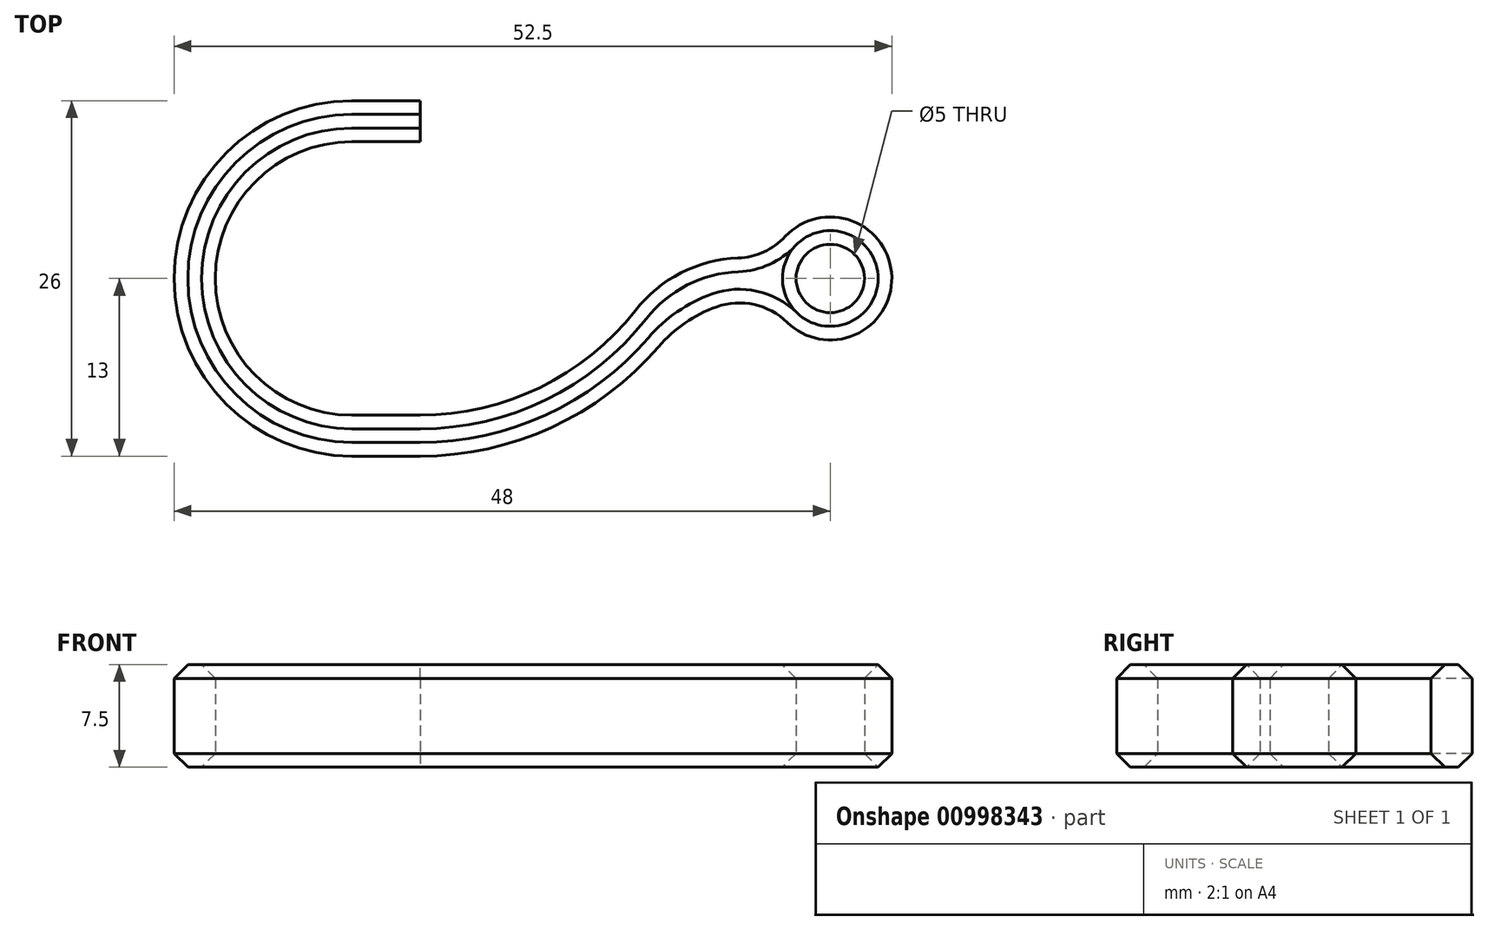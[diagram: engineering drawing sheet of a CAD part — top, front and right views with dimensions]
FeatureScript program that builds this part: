
annotation { "Feature Type Name" : "Feature", "Feature Type Description" : "" }
export const myFeature = defineFeature(function(context is Context, id is Id, definition is map)
    precondition{}
    {
        {
            var Q0;
            Q0=qCreatedBy(makeId("Top.planeOp"),FACE);
            var sketch = newSketch(context, id + "F0", { "sketchPlane" : qUnion([Q0])});
            skArc(sketch, "E0", {"start": v(0, 10) * mm, "mid": v(-10, 0) * mm, "end": v(0, -10) * mm});
            skArc(sketch, "E1", {"start": v(0, 13) * mm, "mid": v(-13, 0) * mm, "end": v(0, -13) * mm});
            skCircle(sketch, "E2", {"center": v(35, 0) * mm, "radius": 2.5 * mm});
            skArc(sketch, "E3", {"start": v(30.76, -1.5) * mm, "mid": v(39.5, 0) * mm, "end": v(30.76, 1.5) * mm});
            skPoint(sketch, "E4.middle", {"position": v(34.86, 0) * mm});
            skLineSegment(sketch, "E5", {"start": v(5, 13) * mm, "end": v(0, 13) * mm});
            skLineSegment(sketch, "E6", {"start": v(5, 10) * mm, "end": v(0, 10) * mm});
            skLineSegment(sketch, "E7", {"start": v(5, 13) * mm, "end": v(5, 10) * mm});
            skArc(sketch, "E8", {"start": v(5, -10) * mm, "mid": v(13.76, -7.98) * mm, "end": v(20.74, -2.33) * mm});
            skLineSegment(sketch, "E9", {"start": v(0, -13) * mm, "end": v(5, -13) * mm});
            skLineSegment(sketch, "E10", {"start": v(5, -10) * mm, "end": v(0, -10) * mm});
            skArc(sketch, "E11", {"start": v(5, -13) * mm, "mid": v(14.6, -10.9) * mm, "end": v(22.45, -4.98) * mm});
            skLineSegment(sketch, "E12.trimOffspring", {"start": v(30.76, 1.5) * mm, "end": v(28.62, 1.5) * mm});
            skLineSegment(sketch, "E13.trimOffspring", {"start": v(30.76, -1.5) * mm, "end": v(30.03, -1.5) * mm});
            skPoint(sketch, "E14.visualSharp", {"position": v(24.92, -1.5) * mm});
            skArc(sketch, "E14.filletArc", {"start": v(30.03, -1.5) * mm, "mid": v(25.86, -2.41) * mm, "end": v(22.45, -4.98) * mm});
            skPoint(sketch, "E15.visualSharp", {"position": v(23.1, 1.5) * mm});
            skArc(sketch, "E15.filletArc", {"start": v(28.62, 1.5) * mm, "mid": v(24.24, 0.5) * mm, "end": v(20.74, -2.33) * mm});
            skSolve(sketch);
        }
        {
            var Q0;
            Q0 = qSketchRegion(id + "F0", true);
            extrude(context, id + "F1", {"entities" : qUnion([Q0]), "endBound" : BoundingType.SYMMETRIC, "depth" : 7.5 * mm, "offsetDistance" : 25 * mm});
        }
        {
            var Q0;
            Q0=makeQuery(id+"F1.opExtrude","SWEPT_EDGE",EDGE,{"disambiguationData":[OSD([sQuery(id+"F0.wireOp",EDGE,"E3"),sQuery(id+"F0.wireOp",EDGE,"E13.trimOffspring")])]});
            var Q1;
            Q1=makeQuery(id+"F1.opExtrude","SWEPT_EDGE",EDGE,{"disambiguationData":[OSD([sQuery(id+"F0.wireOp",EDGE,"E3"),sQuery(id+"F0.wireOp",EDGE,"E12.trimOffspring")])]});
            fillet(context, id + "F2", {"entities" : qUnion([Q0, Q1]), "radius" : 5 * mm, "tangentPropagation" : true, "allowEdgeOverflow" : false});
        }
        {
            var Q0;
            Q0=makeQuery(id+"F1.opExtrude","CAP_EDGE",EDGE,{"disambiguationData":[OSD([sQuery(id+"F0.wireOp",EDGE,"E3")])],"isStart":true});
            var Q1;
            Q1=makeQuery(id+"F1.opExtrude","CAP_EDGE",EDGE,{"disambiguationData":[OSD([sQuery(id+"F0.wireOp",EDGE,"E3")])],"isStart":false});
            var Q2;
            Q2=makeQuery(id+"F1.opExtrude","CAP_EDGE",EDGE,{"disambiguationData":[OSD([sQuery(id+"F0.wireOp",EDGE,"E2")])],"isStart":true});
            var Q3;
            Q3=makeQuery(id+"F1.opExtrude","CAP_EDGE",EDGE,{"disambiguationData":[OSD([sQuery(id+"F0.wireOp",EDGE,"E2")])],"isStart":false});
            chamfer(context, id + "F3", {"entities" : qUnion([Q0, Q1, Q2, Q3]), "width" : 1 * mm, "tangentPropagation" : true});
        }
    });
